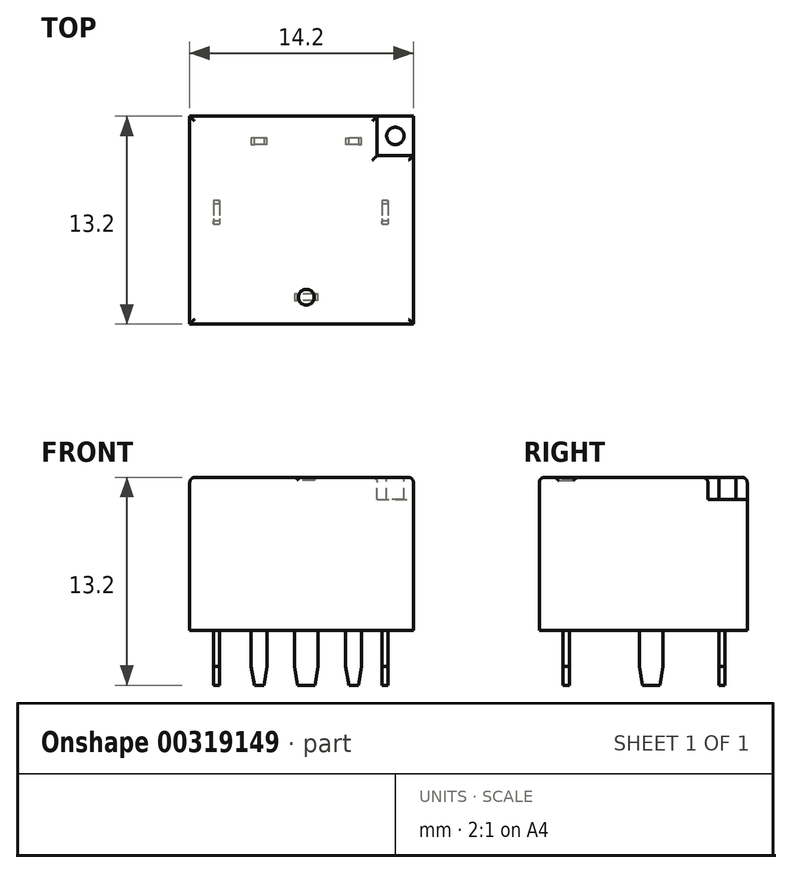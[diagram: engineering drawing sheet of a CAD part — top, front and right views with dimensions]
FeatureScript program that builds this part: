
annotation { "Feature Type Name" : "Feature", "Feature Type Description" : "" }
export const myFeature = defineFeature(function(context is Context, id is Id, definition is map)
    precondition{}
    {
        {
            var Q0;
            Q0=qCreatedBy(makeId("Top.planeOp"),FACE);
            var sketch = newSketch(context, id + "F0", { "sketchPlane" : qUnion([Q0])});
            skLineSegment(sketch, "E0.bottom", {"start": v(-5.5, 0.75) * mm, "end": v(-5.9, 0.75) * mm});
            skLineSegment(sketch, "E0.top", {"start": v(-5.5, -0.75) * mm, "end": v(-5.9, -0.75) * mm});
            skLineSegment(sketch, "E0.left", {"start": v(-5.5, 0.75) * mm, "end": v(-5.5, -0.75) * mm});
            skLineSegment(sketch, "E0.right", {"start": v(-5.9, 0.75) * mm, "end": v(-5.9, -0.75) * mm});
            skPoint(sketch, "E0.middle", {"position": v(-5.7, 0) * mm});
            skLineSegment(sketch, "E1.bottom", {"start": v(5.2, 0.75) * mm, "end": v(4.8, 0.75) * mm});
            skLineSegment(sketch, "E1.top", {"start": v(5.2, -0.75) * mm, "end": v(4.8, -0.75) * mm});
            skLineSegment(sketch, "E1.left", {"start": v(5.2, 0.75) * mm, "end": v(5.2, -0.75) * mm});
            skLineSegment(sketch, "E1.right", {"start": v(4.8, 0.75) * mm, "end": v(4.8, -0.75) * mm});
            skPoint(sketch, "E1.middle", {"position": v(5, 0) * mm});
            skLineSegment(sketch, "E2.bottom", {"start": v(0.75, -5.2) * mm, "end": v(-0.75, -5.2) * mm});
            skLineSegment(sketch, "E2.top", {"start": v(0.75, -5.6) * mm, "end": v(-0.75, -5.6) * mm});
            skLineSegment(sketch, "E2.left", {"start": v(0.75, -5.2) * mm, "end": v(0.75, -5.6) * mm});
            skLineSegment(sketch, "E2.right", {"start": v(-0.75, -5.2) * mm, "end": v(-0.75, -5.6) * mm});
            skPoint(sketch, "E2.middle", {"position": v(0, -5.4) * mm});
            skLineSegment(sketch, "E3.bottom", {"start": v(-2.5, 4.7) * mm, "end": v(-3.5, 4.7) * mm});
            skLineSegment(sketch, "E3.top", {"start": v(-2.5, 4.3) * mm, "end": v(-3.5, 4.3) * mm});
            skLineSegment(sketch, "E3.left", {"start": v(-2.5, 4.7) * mm, "end": v(-2.5, 4.3) * mm});
            skLineSegment(sketch, "E3.right", {"start": v(-3.5, 4.7) * mm, "end": v(-3.5, 4.3) * mm});
            skPoint(sketch, "E3.middle", {"position": v(-3, 4.5) * mm});
            skLineSegment(sketch, "E4.bottom", {"start": v(3.5, 4.3) * mm, "end": v(2.5, 4.3) * mm});
            skLineSegment(sketch, "E4.top", {"start": v(3.5, 4.7) * mm, "end": v(2.5, 4.7) * mm});
            skLineSegment(sketch, "E4.left", {"start": v(3.5, 4.3) * mm, "end": v(3.5, 4.7) * mm});
            skLineSegment(sketch, "E4.right", {"start": v(2.5, 4.3) * mm, "end": v(2.5, 4.7) * mm});
            skPoint(sketch, "E4.middle", {"position": v(3, 4.5) * mm});
            skSolve(sketch);
        }
        {
            var Q0;
            Q0=qCreatedBy(makeId("Top.planeOp"),FACE);
            var sketch = newSketch(context, id + "F1", { "sketchPlane" : qUnion([Q0])});
            skLineSegment(sketch, "E5.bottom", {"start": v(-7.4, -7.1) * mm, "end": v(6.8, -7.1) * mm});
            skLineSegment(sketch, "E5.top", {"start": v(-7.4, 6.1) * mm, "end": v(6.8, 6.1) * mm});
            skLineSegment(sketch, "E5.left", {"start": v(-7.4, -7.1) * mm, "end": v(-7.4, 6.1) * mm});
            skLineSegment(sketch, "E5.right", {"start": v(6.8, -7.1) * mm, "end": v(6.8, 6.1) * mm});
            skSolve(sketch);
        }
        {
            var Q0;
            Q0=makeQuery(id+"F1.imprint","IMPRINT",FACE,{"disambiguationData":[TD([[makeQuery(id+"F1.imprint","IMPRINT",EDGE,{"derivedFrom":sQuery(id+"F1.wireOp",EDGE,"E5.bottom")}),1.0]])]});
            extrude(context, id + "F2", {"entities" : qUnion([Q0]), "depth" : 9.7 * mm});
        }
        {
            var Q0;
            Q0 = qSketchRegion(id + "F0", true);
            extrude(context, id + "F3", {"entities" : qUnion([Q0]), "oppositeDirection" : true, "depth" : 3.5 * mm});
        }
        {
            var Q0;
            Q0=makeQuery(id+"F2.opExtrude","CAP_FACE",FACE,{"disambiguationData":[OSD([sQuery(id+"F1.wireOp",EDGE,"E5.bottom"),sQuery(id+"F1.wireOp",EDGE,"E5.top"),sQuery(id+"F1.wireOp",EDGE,"E5.left"),sQuery(id+"F1.wireOp",EDGE,"E5.right")])],"isStart":false});
            var sketch = newSketch(context, id + "F4", { "sketchPlane" : qUnion([Q0])});
            skCircle(sketch, "E6", {"center": v(5.65, 4.85) * mm, "radius": 0.55 * mm});
            skLineSegment(sketch, "E7.bottom", {"start": v(4.5, 6.1) * mm, "end": v(6.8, 6.1) * mm});
            skLineSegment(sketch, "E7.top", {"start": v(4.5, 3.6) * mm, "end": v(6.8, 3.6) * mm});
            skLineSegment(sketch, "E7.left", {"start": v(4.5, 6.1) * mm, "end": v(4.5, 3.6) * mm});
            skLineSegment(sketch, "E7.right", {"start": v(6.8, 6.1) * mm, "end": v(6.8, 3.6) * mm});
            skCircle(sketch, "E8", {"center": v(0, -5.4) * mm, "radius": 0.5 * mm});
            skPoint(sketch, "E9", {"position": v(5.65, 3.6) * mm});
            skPoint(sketch, "E10", {"position": v(4.5, 4.85) * mm});
            skSolve(sketch);
        }
        {
            var Q0;
            Q0=makeQuery(id+"F4.imprint","IMPRINT",FACE,{"disambiguationData":[TD([[makeQuery(id+"F4.imprint","IMPRINT",EDGE,{"derivedFrom":sQuery(id+"F4.wireOp",EDGE,"E6")}),-1.0]])]});
            extrude(context, id + "F5", {"entities" : qUnion([Q0]), "operationType" : NewBodyOperationType.REMOVE, "oppositeDirection" : true, "depth" : 1.4 * mm});
        }
        {
            var Q0;
            Q0=makeQuery(id+"F4.imprint","IMPRINT",FACE,{"disambiguationData":[TD([[makeQuery(id+"F4.imprint","IMPRINT",EDGE,{"derivedFrom":sQuery(id+"F4.wireOp",EDGE,"E8")}),1.0]])]});
            extrude(context, id + "F6", {"entities" : qUnion([Q0]), "operationType" : NewBodyOperationType.REMOVE, "oppositeDirection" : true, "depth" : 0.2 * mm});
        }
        {
            var Q0;
            {var subQ0=sQuery(id+"F1.wireOp",EDGE,"E5.left");var subQ1=sQuery(id+"F1.wireOp",EDGE,"E5.top");var subQ2=sQuery(id+"F1.wireOp",EDGE,"E5.right");var subQ3=sQuery(id+"F1.wireOp",EDGE,"E5.bottom");Q0=makeQuery(id+"F5.boolean.opBoolean","SPLIT",FACE,{"disambiguationData":[TD([makeQuery(id+"F2.opExtrude","SWEPT_FACE",FACE,{"disambiguationData":[OSD([subQ3])]})])],"derivedFrom":makeQuery(id+"F2.opExtrude","CAP_FACE",FACE,{"disambiguationData":[OSD([subQ3,subQ1,subQ0,subQ2])],"isStart":false})});}
            fillet(context, id + "F7", {"entities" : qUnion([Q0]), "radius" : 0.3 * mm, "tangentPropagation" : true, "allowEdgeOverflow" : false});
        }
        {
            var Q0;
            Q0=makeQuery(id+"F3.opExtrude","CAP_EDGE",EDGE,{"disambiguationData":[OSD([sQuery(id+"F0.wireOp",EDGE,"E0.top")])],"isStart":false});
            var Q1;
            Q1=makeQuery(id+"F3.opExtrude","CAP_EDGE",EDGE,{"disambiguationData":[OSD([sQuery(id+"F0.wireOp",EDGE,"E0.bottom")])],"isStart":false});
            var Q2;
            Q2=makeQuery(id+"F3.opExtrude","CAP_EDGE",EDGE,{"disambiguationData":[OSD([sQuery(id+"F0.wireOp",EDGE,"E2.left")])],"isStart":false});
            var Q3;
            Q3=makeQuery(id+"F3.opExtrude","CAP_EDGE",EDGE,{"disambiguationData":[OSD([sQuery(id+"F0.wireOp",EDGE,"E2.right")])],"isStart":false});
            var Q4;
            Q4=makeQuery(id+"F3.opExtrude","CAP_EDGE",EDGE,{"disambiguationData":[OSD([sQuery(id+"F0.wireOp",EDGE,"E3.left")])],"isStart":false});
            var Q5;
            Q5=makeQuery(id+"F3.opExtrude","CAP_EDGE",EDGE,{"disambiguationData":[OSD([sQuery(id+"F0.wireOp",EDGE,"E3.right")])],"isStart":false});
            var Q6;
            Q6=makeQuery(id+"F3.opExtrude","CAP_EDGE",EDGE,{"disambiguationData":[OSD([sQuery(id+"F0.wireOp",EDGE,"E4.right")])],"isStart":false});
            var Q7;
            Q7=makeQuery(id+"F3.opExtrude","CAP_EDGE",EDGE,{"disambiguationData":[OSD([sQuery(id+"F0.wireOp",EDGE,"E4.left")])],"isStart":false});
            var Q8;
            Q8=makeQuery(id+"F3.opExtrude","CAP_EDGE",EDGE,{"disambiguationData":[OSD([sQuery(id+"F0.wireOp",EDGE,"E1.top")])],"isStart":false});
            var Q9;
            Q9=makeQuery(id+"F3.opExtrude","CAP_EDGE",EDGE,{"disambiguationData":[OSD([sQuery(id+"F0.wireOp",EDGE,"E1.bottom")])],"isStart":false});
            chamfer(context, id + "F8", {"entities" : qUnion([Q0, Q1, Q2, Q3, Q4, Q5, Q6, Q7, Q8, Q9]), "chamferType" : ChamferType.TWO_OFFSETS, "width1" : 0.2 * mm, "oppositeDirection" : false, "width2" : 1.2 * mm, "tangentPropagation" : true});
        }
    });
